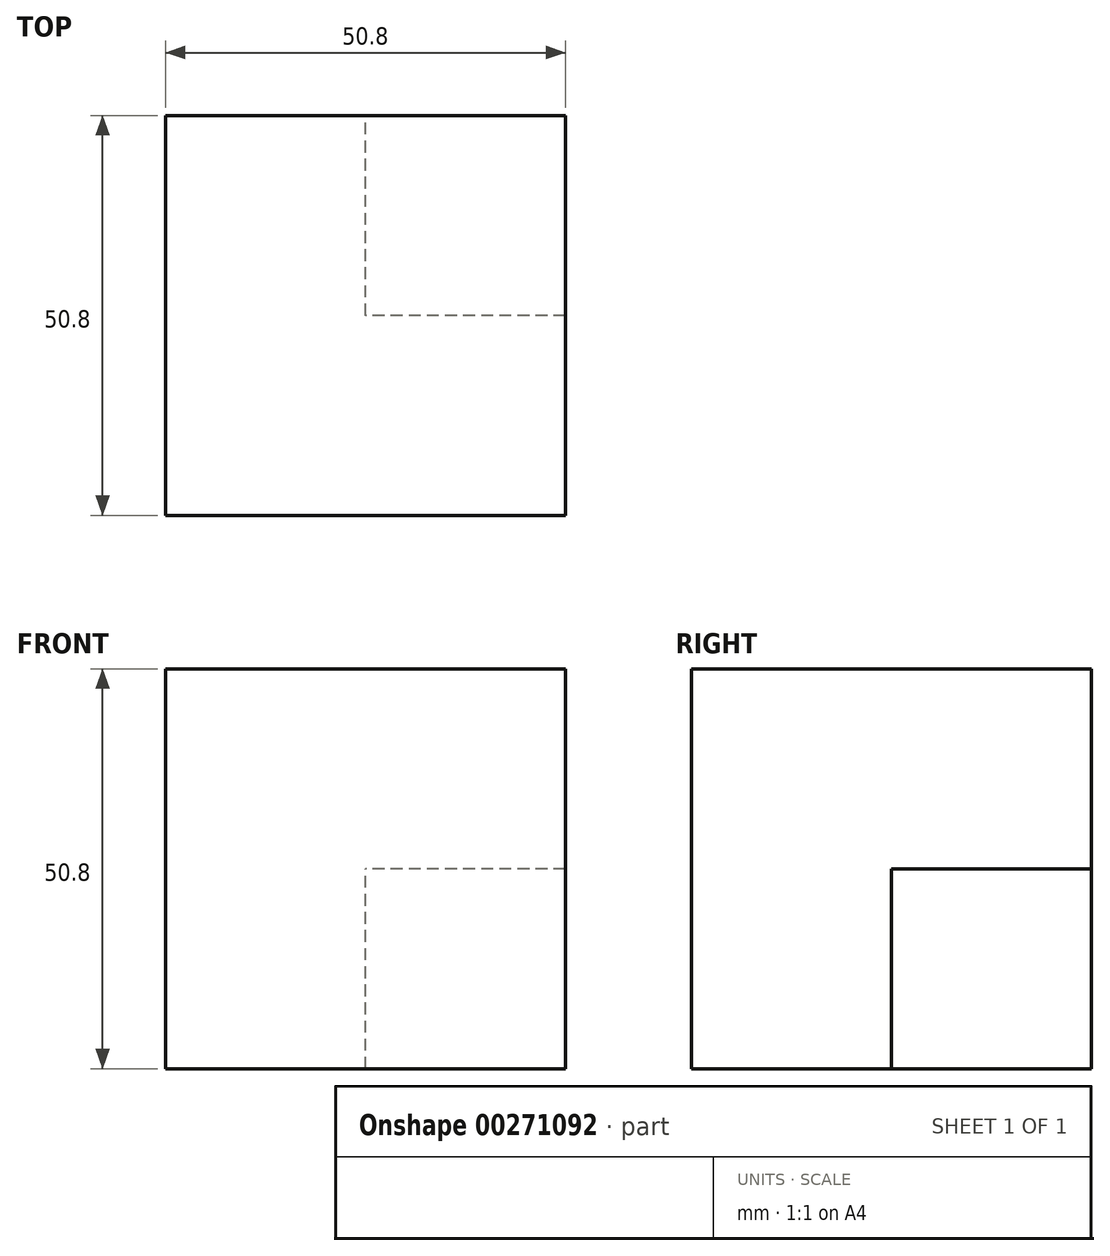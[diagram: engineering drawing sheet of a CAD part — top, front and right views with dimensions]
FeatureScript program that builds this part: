
annotation { "Feature Type Name" : "Feature", "Feature Type Description" : "" }
export const myFeature = defineFeature(function(context is Context, id is Id, definition is map)
    precondition{}
    {
        {
            var Q0;
            Q0=qCreatedBy(makeId("Front.planeOp"),FACE);
            var sketch = newSketch(context, id + "F0", { "sketchPlane" : qUnion([Q0])});
            skLineSegment(sketch, "E0.bottom", {"start": v(0, 0) * mm, "end": v(-50.8, 0) * mm});
            skLineSegment(sketch, "E0.top", {"start": v(0, 50.8) * mm, "end": v(-50.8, 50.8) * mm});
            skLineSegment(sketch, "E0.left", {"start": v(0, 0) * mm, "end": v(0, 50.8) * mm});
            skLineSegment(sketch, "E0.right", {"start": v(-50.8, 0) * mm, "end": v(-50.8, 50.8) * mm});
            skSolve(sketch);
        }
        {
            var Q0;
            Q0=makeQuery(id+"F0.imprint","IMPRINT",FACE,{"disambiguationData":[TD([[makeQuery(id+"F0.imprint","IMPRINT",EDGE,{"derivedFrom":sQuery(id+"F0.wireOp",EDGE,"E0.bottom")}),-1.0]])]});
            var sketch = newSketch(context, id + "F1", { "sketchPlane" : qUnion([Q0])});
            skLineSegment(sketch, "E1.bottom", {"start": v(0, 0) * mm, "end": v(-25.4, 0) * mm});
            skLineSegment(sketch, "E1.top", {"start": v(0, 25.4) * mm, "end": v(-25.4, 25.4) * mm});
            skLineSegment(sketch, "E1.left", {"start": v(0, 0) * mm, "end": v(0, 25.4) * mm});
            skLineSegment(sketch, "E1.right", {"start": v(-25.4, 0) * mm, "end": v(-25.4, 25.4) * mm});
            skSolve(sketch);
        }
        {
            var Q0;
            Q0 = qSketchRegion(id + "F0", true);
            extrude(context, id + "F2", {"entities" : qUnion([Q0]), "depth" : 50.8 * mm});
        }
        {
            var Q0;
            Q0 = qSketchRegion(id + "F1", true);
            extrude(context, id + "F3", {"entities" : qUnion([Q0]), "operationType" : NewBodyOperationType.REMOVE, "depth" : 25.4 * mm});
        }
    });
